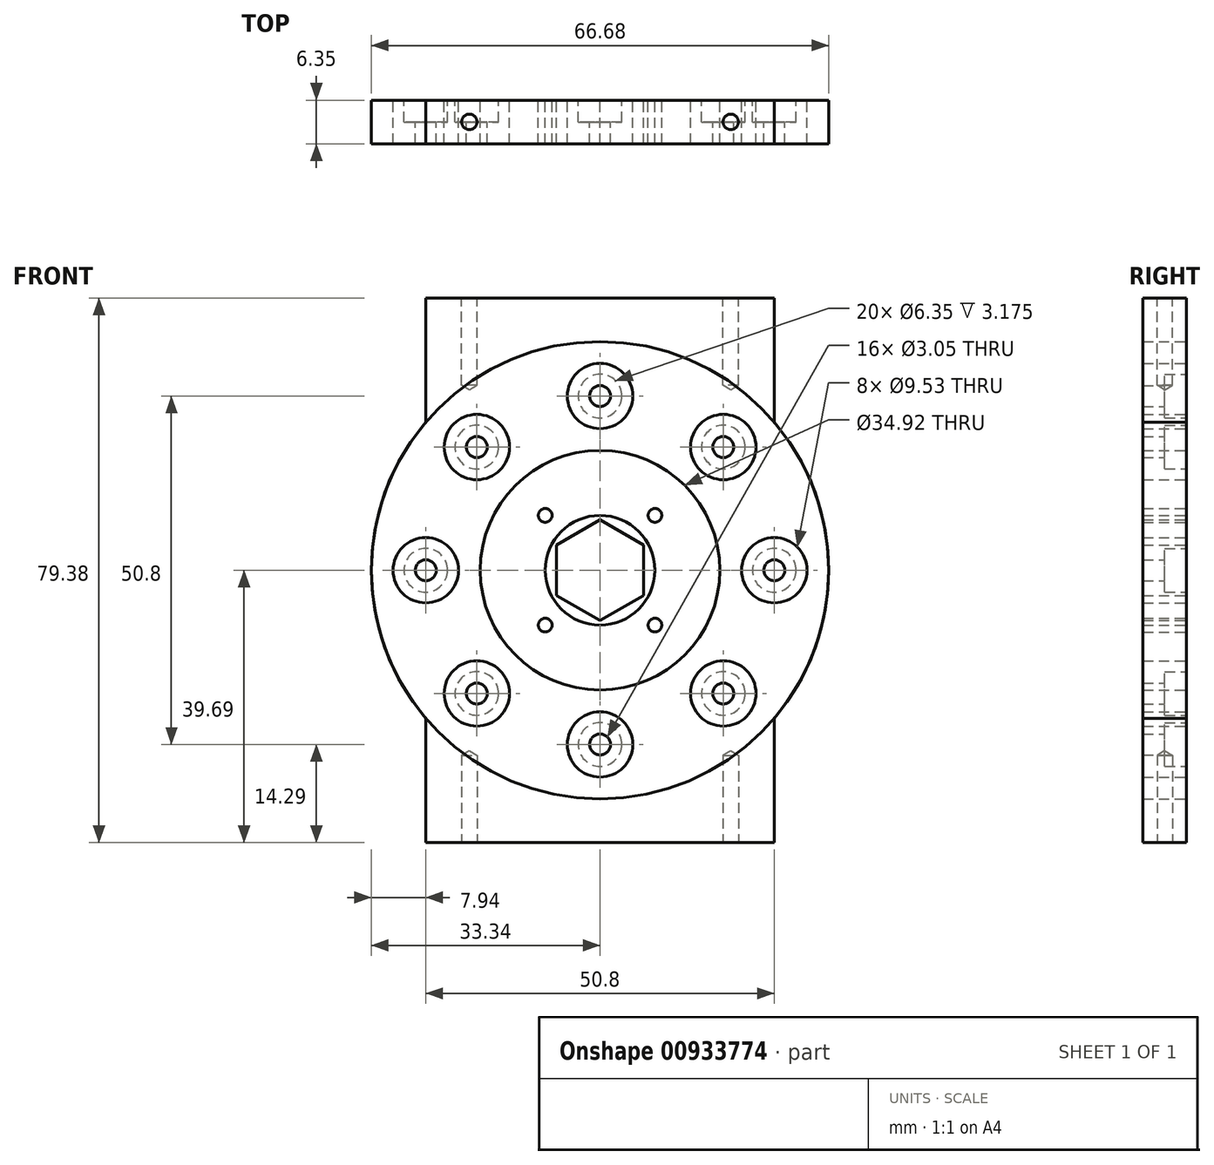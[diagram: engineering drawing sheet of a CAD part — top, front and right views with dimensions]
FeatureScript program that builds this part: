
annotation { "Feature Type Name" : "Feature", "Feature Type Description" : "" }
export const myFeature = defineFeature(function(context is Context, id is Id, definition is map)
    precondition{}
    {
        {
            var Q0;
            Q0=qCreatedBy(makeId("Top.planeOp"),FACE);
            cPlane(context, id + "F0", {"entities" : qUnion([Q0]), "cplaneType" : CPlaneType.OFFSET, "offset" : 39.69 * mm, "width" : 152.4 * mm, "height" : 152.4 * mm});
        }
        {
            var Q0;
            Q0=qCreatedBy(id+"F0.planeOp",FACE);
            cPlane(context, id + "F1", {"entities" : qUnion([Q0]), "cplaneType" : CPlaneType.OFFSET, "offset" : 79.38 * mm, "oppositeDirection" : true, "width" : 152.4 * mm, "height" : 152.4 * mm});
        }
        {
            var Q0;
            Q0=qCreatedBy(makeId("Front.planeOp"),FACE);
            var sketch = newSketch(context, id + "F2", { "sketchPlane" : qUnion([Q0])});
            skCircle(sketch, "E0", {"center": v(0, 0) * mm, "radius": 25.4 * mm, "construction": true});
            skPoint(sketch, "E1", {"position": v(-25.4, 0) * mm});
            skPoint(sketch, "E2.1.0", {"position": v(-17.96, -17.96) * mm});
            skPoint(sketch, "E2.2.0", {"position": v(0, -25.4) * mm});
            skPoint(sketch, "E2.3.0", {"position": v(17.96, -17.96) * mm});
            skPoint(sketch, "E2.4.0", {"position": v(25.4, 0) * mm});
            skPoint(sketch, "E2.5.0", {"position": v(17.96, 17.96) * mm});
            skPoint(sketch, "E2.6.0", {"position": v(0, 25.4) * mm});
            skPoint(sketch, "E2.7.0", {"position": v(-17.96, 17.96) * mm});
            skCircle(sketch, "E3", {"center": v(-17.96, 17.96) * mm, "radius": 3.18 * mm});
            skCircle(sketch, "E4", {"center": v(0, 25.4) * mm, "radius": 3.18 * mm});
            skCircle(sketch, "E5", {"center": v(17.96, 17.96) * mm, "radius": 3.18 * mm});
            skCircle(sketch, "E6", {"center": v(25.4, 0) * mm, "radius": 3.18 * mm});
            skCircle(sketch, "E7", {"center": v(17.96, -17.96) * mm, "radius": 3.18 * mm});
            skCircle(sketch, "E8", {"center": v(0, -25.4) * mm, "radius": 3.18 * mm});
            skCircle(sketch, "E9", {"center": v(-17.96, -17.96) * mm, "radius": 3.18 * mm});
            skCircle(sketch, "E10", {"center": v(-25.4, 0) * mm, "radius": 3.18 * mm});
            skCircle(sketch, "E11", {"center": v(-25.4, 0) * mm, "radius": 4.76 * mm});
            skCircle(sketch, "E12", {"center": v(-17.96, 17.96) * mm, "radius": 4.76 * mm});
            skCircle(sketch, "E13", {"center": v(0, 25.4) * mm, "radius": 4.76 * mm});
            skCircle(sketch, "E14", {"center": v(17.96, 17.96) * mm, "radius": 4.76 * mm});
            skCircle(sketch, "E15", {"center": v(25.4, 0) * mm, "radius": 4.76 * mm});
            skCircle(sketch, "E16", {"center": v(17.96, -17.96) * mm, "radius": 4.76 * mm});
            skCircle(sketch, "E17", {"center": v(0, -25.4) * mm, "radius": 4.76 * mm});
            skCircle(sketch, "E18", {"center": v(-17.96, -17.96) * mm, "radius": 4.76 * mm});
            skCircle(sketch, "E19", {"center": v(0, 0) * mm, "radius": 33.34 * mm});
            skCircle(sketch, "E20", {"center": v(0, 0) * mm, "radius": 17.46 * mm});
            skLineSegment(sketch, "E21", {"start": v(-25.4, -21.6) * mm, "end": v(-25.4, -39.69) * mm});
            skLineSegment(sketch, "E22", {"start": v(-25.4, -39.69) * mm, "end": v(25.4, -39.69) * mm});
            skLineSegment(sketch, "E23", {"start": v(25.4, -39.69) * mm, "end": v(25.4, -21.6) * mm});
            skPoint(sketch, "E24", {"position": v(0, -39.69) * mm});
            skLineSegment(sketch, "E25", {"start": v(25.4, 21.6) * mm, "end": v(25.4, 39.69) * mm});
            skLineSegment(sketch, "E26", {"start": v(25.4, 39.69) * mm, "end": v(-25.4, 39.69) * mm});
            skLineSegment(sketch, "E27", {"start": v(-25.4, 39.69) * mm, "end": v(-25.4, 21.6) * mm});
            skCircle(sketch, "E28", {"center": v(0, 0) * mm, "radius": 8 * mm});
            skCircle(sketch, "E29", {"center": v(-8, 8) * mm, "radius": 1 * mm});
            skCircle(sketch, "E30", {"center": v(-8, -8) * mm, "radius": 1 * mm});
            skCircle(sketch, "E31", {"center": v(8, -8) * mm, "radius": 1 * mm});
            skCircle(sketch, "E32", {"center": v(8, 8) * mm, "radius": 1 * mm});
            skLineSegment(sketch, "E33", {"start": v(-8, 8) * mm, "end": v(-8, -8) * mm, "construction": true});
            skLineSegment(sketch, "E34", {"start": v(-8, -8) * mm, "end": v(8, -8) * mm, "construction": true});
            skLineSegment(sketch, "E35", {"start": v(8, -8) * mm, "end": v(8, 8) * mm, "construction": true});
            skLineSegment(sketch, "E36", {"start": v(8, 8) * mm, "end": v(-8, 8) * mm, "construction": true});
            skPoint(sketch, "E37", {"position": v(0, 8) * mm});
            skPoint(sketch, "E38", {"position": v(8, 0) * mm});
            skCircle(sketch, "E39.cCircle", {"center": v(0, 0) * mm, "radius": 6.35 * mm, "construction": true});
            skLineSegment(sketch, "E39.0", {"start": v(6.35, 3.67) * mm, "end": v(6.35, -3.67) * mm});
            skLineSegment(sketch, "E39.1", {"start": v(6.35, -3.67) * mm, "end": v(0, -7.33) * mm});
            skLineSegment(sketch, "E39.2", {"start": v(0, -7.33) * mm, "end": v(-6.35, -3.67) * mm});
            skLineSegment(sketch, "E39.3", {"start": v(-6.35, -3.67) * mm, "end": v(-6.35, 3.67) * mm});
            skLineSegment(sketch, "E39.4", {"start": v(-6.35, 3.67) * mm, "end": v(0, 7.33) * mm});
            skLineSegment(sketch, "E39.5", {"start": v(0, 7.33) * mm, "end": v(6.35, 3.67) * mm});
            skPoint(sketch, "E39.0.midPoint", {"position": v(6.35, 0) * mm});
            skSolve(sketch);
        }
        {
            var Q0;
            Q0=qCreatedBy(id+"F0.planeOp",FACE);
            var sketch = newSketch(context, id + "F3", { "sketchPlane" : qUnion([Q0])});
            skLineSegment(sketch, "E40.bottom", {"start": v(-25.4, 0) * mm, "end": v(25.4, 0) * mm});
            skLineSegment(sketch, "E40.top", {"start": v(-25.4, -6.35) * mm, "end": v(25.4, -6.35) * mm});
            skLineSegment(sketch, "E40.left", {"start": v(-25.4, 0) * mm, "end": v(-25.4, -6.35) * mm});
            skLineSegment(sketch, "E40.right", {"start": v(25.4, 0) * mm, "end": v(25.4, -6.35) * mm});
            skPoint(sketch, "E41", {"position": v(-25.4, -3.17) * mm});
            skPoint(sketch, "E42", {"position": v(-19.05, -3.17) * mm});
            skPoint(sketch, "E43", {"position": v(25.4, -3.17) * mm});
            skPoint(sketch, "E44", {"position": v(19.05, -3.17) * mm});
            skSolve(sketch);
        }
        {
            var Q0;
            Q0=qCreatedBy(id+"F1.planeOp",FACE);
            var sketch = newSketch(context, id + "F4", { "sketchPlane" : qUnion([Q0])});
            skPoint(sketch, "E45", {"position": v(-19.05, -3.17) * mm});
            skPoint(sketch, "E46", {"position": v(19.05, -3.17) * mm});
            skSolve(sketch);
        }
        {
            var Q0;
            {var subQ0=sQuery(id+"F2.wireOp",EDGE,"E21");Q0=makeQuery(id+"F2.imprint","IMPRINT",FACE,{"disambiguationData":[TD([[makeQuery(id+"F2.imprint","IMPRINT",EDGE,{"derivedFrom":subQ0}),1.0]])]});}
            var Q1;
            Q1=makeQuery(id+"F2.imprint","IMPRINT",FACE,{"disambiguationData":[TD([[makeQuery(id+"F2.imprint","IMPRINT",EDGE,{"derivedFrom":sQuery(id+"F2.wireOp",EDGE,"E11")}),-1.0]])]});
            var Q2;
            Q2=makeQuery(id+"F2.imprint","IMPRINT",FACE,{"disambiguationData":[TD([[makeQuery(id+"F2.imprint","IMPRINT",EDGE,{"derivedFrom":sQuery(id+"F2.wireOp",EDGE,"E8")}),1.0]])]});
            var Q3;
            Q3=makeQuery(id+"F2.imprint","IMPRINT",FACE,{"disambiguationData":[TD([[makeQuery(id+"F2.imprint","IMPRINT",EDGE,{"derivedFrom":sQuery(id+"F2.wireOp",EDGE,"E8")}),-1.0]])]});
            var Q4;
            Q4=makeQuery(id+"F2.imprint","IMPRINT",FACE,{"disambiguationData":[TD([[makeQuery(id+"F2.imprint","IMPRINT",EDGE,{"derivedFrom":sQuery(id+"F2.wireOp",EDGE,"E10")}),-1.0]])]});
            var Q5;
            Q5=makeQuery(id+"F2.imprint","IMPRINT",FACE,{"disambiguationData":[TD([[makeQuery(id+"F2.imprint","IMPRINT",EDGE,{"derivedFrom":sQuery(id+"F2.wireOp",EDGE,"E7")}),-1.0]])]});
            var Q6;
            Q6=makeQuery(id+"F2.imprint","IMPRINT",FACE,{"disambiguationData":[TD([[makeQuery(id+"F2.imprint","IMPRINT",EDGE,{"derivedFrom":sQuery(id+"F2.wireOp",EDGE,"E6")}),-1.0]])]});
            var Q7;
            Q7=makeQuery(id+"F2.imprint","IMPRINT",FACE,{"disambiguationData":[TD([[makeQuery(id+"F2.imprint","IMPRINT",EDGE,{"derivedFrom":sQuery(id+"F2.wireOp",EDGE,"E5")}),-1.0]])]});
            var Q8;
            Q8=makeQuery(id+"F2.imprint","IMPRINT",FACE,{"disambiguationData":[TD([[makeQuery(id+"F2.imprint","IMPRINT",EDGE,{"derivedFrom":sQuery(id+"F2.wireOp",EDGE,"E4")}),-1.0]])]});
            var Q9;
            Q9=makeQuery(id+"F2.imprint","IMPRINT",FACE,{"disambiguationData":[TD([[makeQuery(id+"F2.imprint","IMPRINT",EDGE,{"derivedFrom":sQuery(id+"F2.wireOp",EDGE,"E3")}),-1.0]])]});
            var Q10;
            Q10=makeQuery(id+"F2.imprint","IMPRINT",FACE,{"disambiguationData":[TD([[makeQuery(id+"F2.imprint","IMPRINT",EDGE,{"derivedFrom":sQuery(id+"F2.wireOp",EDGE,"E7")}),1.0]])]});
            var Q11;
            Q11=makeQuery(id+"F2.imprint","IMPRINT",FACE,{"disambiguationData":[TD([[makeQuery(id+"F2.imprint","IMPRINT",EDGE,{"derivedFrom":sQuery(id+"F2.wireOp",EDGE,"E6")}),1.0]])]});
            var Q12;
            Q12=makeQuery(id+"F2.imprint","IMPRINT",FACE,{"disambiguationData":[TD([[makeQuery(id+"F2.imprint","IMPRINT",EDGE,{"derivedFrom":sQuery(id+"F2.wireOp",EDGE,"E10")}),1.0]])]});
            var Q13;
            Q13=makeQuery(id+"F2.imprint","IMPRINT",FACE,{"disambiguationData":[TD([[makeQuery(id+"F2.imprint","IMPRINT",EDGE,{"derivedFrom":sQuery(id+"F2.wireOp",EDGE,"E9")}),-1.0]])]});
            var Q14;
            Q14=makeQuery(id+"F2.imprint","IMPRINT",FACE,{"disambiguationData":[TD([[makeQuery(id+"F2.imprint","IMPRINT",EDGE,{"derivedFrom":sQuery(id+"F2.wireOp",EDGE,"E3")}),1.0]])]});
            var Q15;
            Q15=makeQuery(id+"F2.imprint","IMPRINT",FACE,{"disambiguationData":[TD([[makeQuery(id+"F2.imprint","IMPRINT",EDGE,{"derivedFrom":sQuery(id+"F2.wireOp",EDGE,"E9")}),1.0]])]});
            var Q16;
            Q16=makeQuery(id+"F2.imprint","IMPRINT",FACE,{"disambiguationData":[TD([[makeQuery(id+"F2.imprint","IMPRINT",EDGE,{"derivedFrom":sQuery(id+"F2.wireOp",EDGE,"E4")}),1.0]])]});
            var Q17;
            Q17=makeQuery(id+"F2.imprint","IMPRINT",FACE,{"disambiguationData":[TD([[makeQuery(id+"F2.imprint","IMPRINT",EDGE,{"derivedFrom":sQuery(id+"F2.wireOp",EDGE,"E5")}),1.0]])]});
            var Q18;
            {var subQ0=sQuery(id+"F2.wireOp",EDGE,"E25");Q18=makeQuery(id+"F2.imprint","IMPRINT",FACE,{"disambiguationData":[TD([[makeQuery(id+"F2.imprint","IMPRINT",EDGE,{"derivedFrom":subQ0}),1.0]])]});}
            extrude(context, id + "F5", {"entities" : qUnion([Q0, Q1, Q2, Q3, Q4, Q5, Q6, Q7, Q8, Q9, Q10, Q11, Q12, Q13, Q14, Q15, Q16, Q17, Q18]), "depth" : 6.35 * mm, "offsetDistance" : 25.4 * mm});
        }
        {
            var Q0;
            Q0=makeQuery(id+"F2.imprint","IMPRINT",FACE,{"disambiguationData":[TD([[makeQuery(id+"F2.imprint","IMPRINT",EDGE,{"derivedFrom":sQuery(id+"F2.wireOp",EDGE,"E7")}),1.0]])]});
            var Q1;
            Q1=makeQuery(id+"F2.imprint","IMPRINT",FACE,{"disambiguationData":[TD([[makeQuery(id+"F2.imprint","IMPRINT",EDGE,{"derivedFrom":sQuery(id+"F2.wireOp",EDGE,"E5")}),1.0]])]});
            var Q2;
            Q2=makeQuery(id+"F2.imprint","IMPRINT",FACE,{"disambiguationData":[TD([[makeQuery(id+"F2.imprint","IMPRINT",EDGE,{"derivedFrom":sQuery(id+"F2.wireOp",EDGE,"E3")}),1.0]])]});
            var Q3;
            Q3=makeQuery(id+"F2.imprint","IMPRINT",FACE,{"disambiguationData":[TD([[makeQuery(id+"F2.imprint","IMPRINT",EDGE,{"derivedFrom":sQuery(id+"F2.wireOp",EDGE,"E9")}),1.0]])]});
            var Q4;
            Q4=sQuery(id+"F2.wireOp",EDGE,"E9");
            var Q5;
            Q5=sQuery(id+"F2.wireOp",EDGE,"E3");
            var Q6;
            Q6=sQuery(id+"F2.wireOp",EDGE,"E5");
            var Q7;
            Q7=sQuery(id+"F2.wireOp",EDGE,"E7");
            extrude(context, id + "F6", {"entities" : qUnion([Q0, Q1, Q2, Q3]), "operationType" : NewBodyOperationType.REMOVE, "surfaceEntities" : qUnion([Q4, Q5, Q6, Q7]), "depth" : 3.17 * mm, "offsetDistance" : 25.4 * mm});
        }
        {
            var Q0;
            Q0=sQuery(id+"F2.wireOp",VERTEX,"E2.5.0");
            var Q1;
            Q1=sQuery(id+"F2.wireOp",VERTEX,"E2.7.0");
            var Q2;
            Q2=sQuery(id+"F2.wireOp",VERTEX,"E2.1.0");
            var Q3;
            Q3=sQuery(id+"F2.wireOp",VERTEX,"E2.3.0");
            var Q4;
            Q4=makeQuery(id+"F5.opExtrude","SWEPT_BODY",BODY,{"disambiguationData":[OSD([sQuery(id+"F2.wireOp",EDGE,"E19"),sQuery(id+"F2.wireOp",EDGE,"E20"),sQuery(id+"F2.wireOp",EDGE,"E21"),sQuery(id+"F2.wireOp",EDGE,"E22"),sQuery(id+"F2.wireOp",EDGE,"E23"),sQuery(id+"F2.wireOp",EDGE,"E25"),sQuery(id+"F2.wireOp",EDGE,"E26"),sQuery(id+"F2.wireOp",EDGE,"E27")])]});
            hole(context, id + "F7", {"style" : HoleStyle.SIMPLE, "endStyle" : HoleEndStyle.THROUGH, "oppositeDirection" : true, "standardTappedOrClearance" : lookupTablePath({ "fit" : "Close (ASME)", "standard" : "ANSI", "size" : "#4", "type" : "Clearance" }), "standardBlindInLast" : lookupTablePath({ "fit" : "Close", "standard" : "ANSI", "engagement" : "75%", "pitch" : "40 tpi", "size" : "#4", "type" : "Clearance & tapped" }), "holeDiameter" : 3.05 * mm, "majorDiameter" : 6.35 * mm, "isTappedThrough" : true, "tappedDepth" : 12.7 * mm, "tapClearance" : 3, "locations" : qUnion([Q0, Q1, Q2, Q3]), "scope" : qUnion([Q4])});
        }
        {
            var Q0;
            Q0=sQuery(id+"F3.wireOp",VERTEX,"E42");
            var Q1;
            Q1=sQuery(id+"F3.wireOp",VERTEX,"E44");
            var Q2;
            Q2=makeQuery(id+"F5.opExtrude","SWEPT_BODY",BODY,{"disambiguationData":[OSD([sQuery(id+"F2.wireOp",EDGE,"E19"),sQuery(id+"F2.wireOp",EDGE,"E20"),sQuery(id+"F2.wireOp",EDGE,"E21"),sQuery(id+"F2.wireOp",EDGE,"E22"),sQuery(id+"F2.wireOp",EDGE,"E23"),sQuery(id+"F2.wireOp",EDGE,"E25"),sQuery(id+"F2.wireOp",EDGE,"E26"),sQuery(id+"F2.wireOp",EDGE,"E27")])]});
            hole(context, id + "F8", {"style" : HoleStyle.SIMPLE, "endStyle" : HoleEndStyle.BLIND, "standardTappedOrClearance" : lookupTablePath({ "standard" : "ANSI", "engagement" : "75%", "pitch" : "40 tpi", "size" : "#4", "type" : "Tapped" }), "standardBlindInLast" : lookupTablePath({ "standard" : "ANSI", "fit" : "Normal", "engagement" : "75%", "pitch" : "40 tpi", "size" : "#4", "type" : "Clearance & tapped" }), "holeDiameter" : 2.26 * mm, "majorDiameter" : 2.84 * mm, "showTappedDepth" : true, "holeDepth" : 12.7 * mm, "isTappedThrough" : true, "tappedDepth" : 10.8 * mm, "tapClearance" : 3, "locations" : qUnion([Q0, Q1]), "scope" : qUnion([Q2])});
        }
        {
            var Q0;
            Q0=sQuery(id+"F4.wireOp",VERTEX,"E45");
            var Q1;
            Q1=sQuery(id+"F4.wireOp",VERTEX,"E46");
            var Q2;
            Q2=makeQuery(id+"F5.opExtrude","SWEPT_BODY",BODY,{"disambiguationData":[OSD([sQuery(id+"F2.wireOp",EDGE,"E19"),sQuery(id+"F2.wireOp",EDGE,"E20"),sQuery(id+"F2.wireOp",EDGE,"E21"),sQuery(id+"F2.wireOp",EDGE,"E22"),sQuery(id+"F2.wireOp",EDGE,"E23"),sQuery(id+"F2.wireOp",EDGE,"E25"),sQuery(id+"F2.wireOp",EDGE,"E26"),sQuery(id+"F2.wireOp",EDGE,"E27")])]});
            hole(context, id + "F9", {"style" : HoleStyle.SIMPLE, "endStyle" : HoleEndStyle.BLIND, "oppositeDirection" : true, "standardTappedOrClearance" : lookupTablePath({ "standard" : "ANSI", "engagement" : "75%", "pitch" : "40 tpi", "size" : "#4", "type" : "Tapped" }), "standardBlindInLast" : lookupTablePath({ "standard" : "ANSI", "fit" : "Normal", "engagement" : "75%", "pitch" : "40 tpi", "size" : "#4", "type" : "Clearance & tapped" }), "holeDiameter" : 2.26 * mm, "majorDiameter" : 2.84 * mm, "showTappedDepth" : true, "holeDepth" : 12.7 * mm, "isTappedThrough" : true, "tappedDepth" : 10.8 * mm, "tapClearance" : 3, "locations" : qUnion([Q0, Q1]), "scope" : qUnion([Q2])});
        }
        {
            var Q0;
            Q0=makeQuery(id+"F2.imprint","IMPRINT",FACE,{"disambiguationData":[TD([[makeQuery(id+"F2.imprint","IMPRINT",EDGE,{"derivedFrom":sQuery(id+"F2.wireOp",EDGE,"E10")}),1.0]])]});
            var Q1;
            Q1=makeQuery(id+"F2.imprint","IMPRINT",FACE,{"disambiguationData":[TD([[makeQuery(id+"F2.imprint","IMPRINT",EDGE,{"derivedFrom":sQuery(id+"F2.wireOp",EDGE,"E10")}),-1.0]])]});
            var Q2;
            Q2=makeQuery(id+"F2.imprint","IMPRINT",FACE,{"disambiguationData":[TD([[makeQuery(id+"F2.imprint","IMPRINT",EDGE,{"derivedFrom":sQuery(id+"F2.wireOp",EDGE,"E8")}),1.0]])]});
            var Q3;
            Q3=makeQuery(id+"F2.imprint","IMPRINT",FACE,{"disambiguationData":[TD([[makeQuery(id+"F2.imprint","IMPRINT",EDGE,{"derivedFrom":sQuery(id+"F2.wireOp",EDGE,"E8")}),-1.0]])]});
            var Q4;
            Q4=makeQuery(id+"F2.imprint","IMPRINT",FACE,{"disambiguationData":[TD([[makeQuery(id+"F2.imprint","IMPRINT",EDGE,{"derivedFrom":sQuery(id+"F2.wireOp",EDGE,"E6")}),-1.0]])]});
            var Q5;
            Q5=makeQuery(id+"F2.imprint","IMPRINT",FACE,{"disambiguationData":[TD([[makeQuery(id+"F2.imprint","IMPRINT",EDGE,{"derivedFrom":sQuery(id+"F2.wireOp",EDGE,"E6")}),1.0]])]});
            var Q6;
            Q6=makeQuery(id+"F2.imprint","IMPRINT",FACE,{"disambiguationData":[TD([[makeQuery(id+"F2.imprint","IMPRINT",EDGE,{"derivedFrom":sQuery(id+"F2.wireOp",EDGE,"E4")}),1.0]])]});
            var Q7;
            Q7=makeQuery(id+"F2.imprint","IMPRINT",FACE,{"disambiguationData":[TD([[makeQuery(id+"F2.imprint","IMPRINT",EDGE,{"derivedFrom":sQuery(id+"F2.wireOp",EDGE,"E4")}),-1.0]])]});
            var Q8;
            Q8=makeQuery(id+"F2.imprint","IMPRINT",FACE,{"disambiguationData":[TD([[makeQuery(id+"F2.imprint","IMPRINT",EDGE,{"derivedFrom":sQuery(id+"F2.wireOp",EDGE,"E11")}),-1.0]])]});
            var Q9;
            Q9=makeQuery(id+"F2.imprint","IMPRINT",FACE,{"disambiguationData":[TD([[makeQuery(id+"F2.imprint","IMPRINT",EDGE,{"derivedFrom":sQuery(id+"F2.wireOp",EDGE,"E20")}),1.0]])]});
            extrude(context, id + "F10", {"entities" : qUnion([Q0, Q1, Q2, Q3, Q4, Q5, Q6, Q7, Q8, Q9]), "depth" : 6.35 * mm, "offsetDistance" : 25.4 * mm});
        }
        {
            var Q0;
            Q0=makeQuery(id+"F2.imprint","IMPRINT",FACE,{"disambiguationData":[TD([[makeQuery(id+"F2.imprint","IMPRINT",EDGE,{"derivedFrom":sQuery(id+"F2.wireOp",EDGE,"E4")}),1.0]])]});
            var Q1;
            Q1=makeQuery(id+"F2.imprint","IMPRINT",FACE,{"disambiguationData":[TD([[makeQuery(id+"F2.imprint","IMPRINT",EDGE,{"derivedFrom":sQuery(id+"F2.wireOp",EDGE,"E10")}),1.0]])]});
            var Q2;
            Q2=makeQuery(id+"F2.imprint","IMPRINT",FACE,{"disambiguationData":[TD([[makeQuery(id+"F2.imprint","IMPRINT",EDGE,{"derivedFrom":sQuery(id+"F2.wireOp",EDGE,"E8")}),1.0]])]});
            var Q3;
            Q3=makeQuery(id+"F2.imprint","IMPRINT",FACE,{"disambiguationData":[TD([[makeQuery(id+"F2.imprint","IMPRINT",EDGE,{"derivedFrom":sQuery(id+"F2.wireOp",EDGE,"E6")}),1.0]])]});
            var Q4;
            Q4=sQuery(id+"F2.wireOp",EDGE,"E10");
            var Q5;
            Q5=sQuery(id+"F2.wireOp",EDGE,"E6");
            var Q6;
            Q6=sQuery(id+"F2.wireOp",EDGE,"E8");
            var Q7;
            Q7=sQuery(id+"F2.wireOp",EDGE,"E4");
            extrude(context, id + "F11", {"entities" : qUnion([Q0, Q1, Q2, Q3]), "operationType" : NewBodyOperationType.REMOVE, "surfaceEntities" : qUnion([Q4, Q5, Q6, Q7]), "depth" : 3.17 * mm, "offsetDistance" : 25.4 * mm});
        }
        {
            var Q0;
            Q0=sQuery(id+"F2.wireOp",VERTEX,"E2.4.0");
            var Q1;
            Q1=sQuery(id+"F2.wireOp",VERTEX,"E2.6.0");
            var Q2;
            Q2=sQuery(id+"F2.wireOp",VERTEX,"E1");
            var Q3;
            Q3=sQuery(id+"F2.wireOp",VERTEX,"E2.2.0");
            var Q4;
            Q4=makeQuery(id+"F10.opExtrude","SWEPT_BODY",BODY,{"disambiguationData":[OSD([sQuery(id+"F2.wireOp",EDGE,"E12"),sQuery(id+"F2.wireOp",EDGE,"E14"),sQuery(id+"F2.wireOp",EDGE,"E16"),sQuery(id+"F2.wireOp",EDGE,"E18"),sQuery(id+"F2.wireOp",EDGE,"E19"),sQuery(id+"F2.wireOp",EDGE,"E28"),sQuery(id+"F2.wireOp",EDGE,"E29"),sQuery(id+"F2.wireOp",EDGE,"E30"),sQuery(id+"F2.wireOp",EDGE,"E31"),sQuery(id+"F2.wireOp",EDGE,"E32")])]});
            hole(context, id + "F12", {"style" : HoleStyle.SIMPLE, "endStyle" : HoleEndStyle.THROUGH, "oppositeDirection" : true, "standardTappedOrClearance" : lookupTablePath({ "fit" : "Close (ASME)", "standard" : "ANSI", "size" : "#4", "type" : "Clearance" }), "standardBlindInLast" : lookupTablePath({ "fit" : "Close", "standard" : "ANSI", "engagement" : "75%", "pitch" : "40 tpi", "size" : "#4", "type" : "Clearance & tapped" }), "holeDiameter" : 3.05 * mm, "majorDiameter" : 6.35 * mm, "isTappedThrough" : true, "tappedDepth" : 12.7 * mm, "tapClearance" : 3, "locations" : qUnion([Q0, Q1, Q2, Q3]), "scope" : qUnion([Q4])});
        }
        {
            var Q0;
            {var subQ0=sQuery(id+"F2.wireOp",EDGE,"E25");Q0=makeQuery(id+"F2.imprint","IMPRINT",FACE,{"disambiguationData":[TD([[makeQuery(id+"F2.imprint","IMPRINT",EDGE,{"derivedFrom":subQ0}),1.0]])]});}
            var Q1;
            Q1=makeQuery(id+"F2.imprint","IMPRINT",FACE,{"disambiguationData":[TD([[makeQuery(id+"F2.imprint","IMPRINT",EDGE,{"derivedFrom":sQuery(id+"F2.wireOp",EDGE,"E11")}),-1.0]])]});
            var Q2;
            Q2=makeQuery(id+"F2.imprint","IMPRINT",FACE,{"disambiguationData":[TD([[makeQuery(id+"F2.imprint","IMPRINT",EDGE,{"derivedFrom":sQuery(id+"F2.wireOp",EDGE,"E5")}),-1.0]])]});
            var Q3;
            Q3=makeQuery(id+"F2.imprint","IMPRINT",FACE,{"disambiguationData":[TD([[makeQuery(id+"F2.imprint","IMPRINT",EDGE,{"derivedFrom":sQuery(id+"F2.wireOp",EDGE,"E5")}),1.0]])]});
            var Q4;
            Q4=makeQuery(id+"F2.imprint","IMPRINT",FACE,{"disambiguationData":[TD([[makeQuery(id+"F2.imprint","IMPRINT",EDGE,{"derivedFrom":sQuery(id+"F2.wireOp",EDGE,"E28")}),1.0]])]});
            var Q5;
            Q5=makeQuery(id+"F2.imprint","IMPRINT",FACE,{"disambiguationData":[TD([[makeQuery(id+"F2.imprint","IMPRINT",EDGE,{"derivedFrom":sQuery(id+"F2.wireOp",EDGE,"E20")}),1.0]])]});
            var Q6;
            Q6=makeQuery(id+"F2.imprint","IMPRINT",FACE,{"disambiguationData":[TD([[makeQuery(id+"F2.imprint","IMPRINT",EDGE,{"derivedFrom":sQuery(id+"F2.wireOp",EDGE,"E7")}),1.0]])]});
            var Q7;
            Q7=makeQuery(id+"F2.imprint","IMPRINT",FACE,{"disambiguationData":[TD([[makeQuery(id+"F2.imprint","IMPRINT",EDGE,{"derivedFrom":sQuery(id+"F2.wireOp",EDGE,"E7")}),-1.0]])]});
            var Q8;
            Q8=makeQuery(id+"F2.imprint","IMPRINT",FACE,{"disambiguationData":[TD([[makeQuery(id+"F2.imprint","IMPRINT",EDGE,{"derivedFrom":sQuery(id+"F2.wireOp",EDGE,"E9")}),-1.0]])]});
            var Q9;
            {var subQ0=sQuery(id+"F2.wireOp",EDGE,"E21");Q9=makeQuery(id+"F2.imprint","IMPRINT",FACE,{"disambiguationData":[TD([[makeQuery(id+"F2.imprint","IMPRINT",EDGE,{"derivedFrom":subQ0}),1.0]])]});}
            var Q10;
            Q10=makeQuery(id+"F2.imprint","IMPRINT",FACE,{"disambiguationData":[TD([[makeQuery(id+"F2.imprint","IMPRINT",EDGE,{"derivedFrom":sQuery(id+"F2.wireOp",EDGE,"E3")}),-1.0]])]});
            var Q11;
            Q11=makeQuery(id+"F2.imprint","IMPRINT",FACE,{"disambiguationData":[TD([[makeQuery(id+"F2.imprint","IMPRINT",EDGE,{"derivedFrom":sQuery(id+"F2.wireOp",EDGE,"E3")}),1.0]])]});
            var Q12;
            Q12=makeQuery(id+"F2.imprint","IMPRINT",FACE,{"disambiguationData":[TD([[makeQuery(id+"F2.imprint","IMPRINT",EDGE,{"derivedFrom":sQuery(id+"F2.wireOp",EDGE,"E9")}),1.0]])]});
            var Q13;
            Q13=makeQuery(id+"F2.imprint","IMPRINT",FACE,{"disambiguationData":[TD([[makeQuery(id+"F2.imprint","IMPRINT",EDGE,{"derivedFrom":sQuery(id+"F2.wireOp",EDGE,"E31")}),1.0]])]});
            var Q14;
            Q14=makeQuery(id+"F2.imprint","IMPRINT",FACE,{"disambiguationData":[TD([[makeQuery(id+"F2.imprint","IMPRINT",EDGE,{"derivedFrom":sQuery(id+"F2.wireOp",EDGE,"E29")}),1.0]])]});
            var Q15;
            Q15=makeQuery(id+"F2.imprint","IMPRINT",FACE,{"disambiguationData":[TD([[makeQuery(id+"F2.imprint","IMPRINT",EDGE,{"derivedFrom":sQuery(id+"F2.wireOp",EDGE,"E32")}),1.0]])]});
            var Q16;
            Q16=makeQuery(id+"F2.imprint","IMPRINT",FACE,{"disambiguationData":[TD([[makeQuery(id+"F2.imprint","IMPRINT",EDGE,{"derivedFrom":sQuery(id+"F2.wireOp",EDGE,"E30")}),1.0]])]});
            extrude(context, id + "F13", {"entities" : qUnion([Q0, Q1, Q2, Q3, Q4, Q5, Q6, Q7, Q8, Q9, Q10, Q11, Q12, Q13, Q14, Q15, Q16]), "depth" : 6.35 * mm, "offsetDistance" : 25.4 * mm});
        }
        {
            var Q0;
            Q0=makeQuery(id+"F2.imprint","IMPRINT",FACE,{"disambiguationData":[TD([[makeQuery(id+"F2.imprint","IMPRINT",EDGE,{"derivedFrom":sQuery(id+"F2.wireOp",EDGE,"E7")}),1.0]])]});
            var Q1;
            Q1=makeQuery(id+"F2.imprint","IMPRINT",FACE,{"disambiguationData":[TD([[makeQuery(id+"F2.imprint","IMPRINT",EDGE,{"derivedFrom":sQuery(id+"F2.wireOp",EDGE,"E5")}),1.0]])]});
            var Q2;
            Q2=makeQuery(id+"F2.imprint","IMPRINT",FACE,{"disambiguationData":[TD([[makeQuery(id+"F2.imprint","IMPRINT",EDGE,{"derivedFrom":sQuery(id+"F2.wireOp",EDGE,"E3")}),1.0]])]});
            var Q3;
            Q3=makeQuery(id+"F2.imprint","IMPRINT",FACE,{"disambiguationData":[TD([[makeQuery(id+"F2.imprint","IMPRINT",EDGE,{"derivedFrom":sQuery(id+"F2.wireOp",EDGE,"E9")}),1.0]])]});
            extrude(context, id + "F14", {"entities" : qUnion([Q0, Q1, Q2, Q3]), "operationType" : NewBodyOperationType.REMOVE, "depth" : 3.17 * mm, "offsetDistance" : 25.4 * mm});
        }
        {
            var Q0;
            Q0=sQuery(id+"F2.wireOp",VERTEX,"E2.5.0");
            var Q1;
            Q1=sQuery(id+"F2.wireOp",VERTEX,"E2.7.0");
            var Q2;
            Q2=sQuery(id+"F2.wireOp",VERTEX,"E2.1.0");
            var Q3;
            Q3=sQuery(id+"F2.wireOp",VERTEX,"E2.3.0");
            var Q4;
            Q4=makeQuery(id+"F13.opExtrude","SWEPT_BODY",BODY,{"disambiguationData":[OSD([sQuery(id+"F2.wireOp",EDGE,"E11"),sQuery(id+"F2.wireOp",EDGE,"E13"),sQuery(id+"F2.wireOp",EDGE,"E15"),sQuery(id+"F2.wireOp",EDGE,"E17"),sQuery(id+"F2.wireOp",EDGE,"E19"),sQuery(id+"F2.wireOp",EDGE,"E21"),sQuery(id+"F2.wireOp",EDGE,"E22"),sQuery(id+"F2.wireOp",EDGE,"E23"),sQuery(id+"F2.wireOp",EDGE,"E25"),sQuery(id+"F2.wireOp",EDGE,"E26"),sQuery(id+"F2.wireOp",EDGE,"E27")])]});
            hole(context, id + "F15", {"style" : HoleStyle.SIMPLE, "endStyle" : HoleEndStyle.THROUGH, "oppositeDirection" : true, "standardTappedOrClearance" : lookupTablePath({ "fit" : "Close (ASME)", "standard" : "ANSI", "size" : "#4", "type" : "Clearance" }), "standardBlindInLast" : lookupTablePath({ "fit" : "Close", "standard" : "ANSI", "engagement" : "75%", "pitch" : "40 tpi", "size" : "#4", "type" : "Clearance & tapped" }), "holeDiameter" : 3.05 * mm, "majorDiameter" : 6.35 * mm, "isTappedThrough" : true, "tappedDepth" : 12.7 * mm, "tapClearance" : 3, "locations" : qUnion([Q0, Q1, Q2, Q3]), "scope" : qUnion([Q4])});
        }
        {
            var Q0;
            Q0=sQuery(id+"F3.wireOp",VERTEX,"E42");
            var Q1;
            Q1=sQuery(id+"F3.wireOp",VERTEX,"E44");
            var Q2;
            Q2=makeQuery(id+"F13.opExtrude","SWEPT_BODY",BODY,{"disambiguationData":[OSD([sQuery(id+"F2.wireOp",EDGE,"E11"),sQuery(id+"F2.wireOp",EDGE,"E13"),sQuery(id+"F2.wireOp",EDGE,"E15"),sQuery(id+"F2.wireOp",EDGE,"E17"),sQuery(id+"F2.wireOp",EDGE,"E19"),sQuery(id+"F2.wireOp",EDGE,"E21"),sQuery(id+"F2.wireOp",EDGE,"E22"),sQuery(id+"F2.wireOp",EDGE,"E23"),sQuery(id+"F2.wireOp",EDGE,"E25"),sQuery(id+"F2.wireOp",EDGE,"E26"),sQuery(id+"F2.wireOp",EDGE,"E27"),sQuery(id+"F2.wireOp",EDGE,"E39.0"),sQuery(id+"F2.wireOp",EDGE,"E39.1"),sQuery(id+"F2.wireOp",EDGE,"E39.2"),sQuery(id+"F2.wireOp",EDGE,"E39.3"),sQuery(id+"F2.wireOp",EDGE,"E39.4"),sQuery(id+"F2.wireOp",EDGE,"E39.5")])]});
            hole(context, id + "F16", {"style" : HoleStyle.SIMPLE, "endStyle" : HoleEndStyle.BLIND, "standardTappedOrClearance" : lookupTablePath({ "standard" : "ANSI", "engagement" : "75%", "pitch" : "40 tpi", "size" : "#4", "type" : "Tapped" }), "standardBlindInLast" : lookupTablePath({ "standard" : "ANSI", "fit" : "Normal", "engagement" : "75%", "pitch" : "40 tpi", "size" : "#4", "type" : "Clearance & tapped" }), "holeDiameter" : 2.26 * mm, "majorDiameter" : 2.84 * mm, "showTappedDepth" : true, "holeDepth" : 12.7 * mm, "isTappedThrough" : true, "tappedDepth" : 10.8 * mm, "tapClearance" : 3, "locations" : qUnion([Q0, Q1]), "scope" : qUnion([Q2])});
        }
        {
            var Q0;
            Q0=sQuery(id+"F4.wireOp",VERTEX,"E45");
            var Q1;
            Q1=sQuery(id+"F4.wireOp",VERTEX,"E46");
            var Q2;
            Q2=makeQuery(id+"F13.opExtrude","SWEPT_BODY",BODY,{"disambiguationData":[OSD([sQuery(id+"F2.wireOp",EDGE,"E11"),sQuery(id+"F2.wireOp",EDGE,"E13"),sQuery(id+"F2.wireOp",EDGE,"E15"),sQuery(id+"F2.wireOp",EDGE,"E17"),sQuery(id+"F2.wireOp",EDGE,"E19"),sQuery(id+"F2.wireOp",EDGE,"E21"),sQuery(id+"F2.wireOp",EDGE,"E22"),sQuery(id+"F2.wireOp",EDGE,"E23"),sQuery(id+"F2.wireOp",EDGE,"E25"),sQuery(id+"F2.wireOp",EDGE,"E26"),sQuery(id+"F2.wireOp",EDGE,"E27"),sQuery(id+"F2.wireOp",EDGE,"E39.0"),sQuery(id+"F2.wireOp",EDGE,"E39.1"),sQuery(id+"F2.wireOp",EDGE,"E39.2"),sQuery(id+"F2.wireOp",EDGE,"E39.3"),sQuery(id+"F2.wireOp",EDGE,"E39.4"),sQuery(id+"F2.wireOp",EDGE,"E39.5")])]});
            hole(context, id + "F17", {"style" : HoleStyle.SIMPLE, "endStyle" : HoleEndStyle.BLIND, "oppositeDirection" : true, "standardTappedOrClearance" : lookupTablePath({ "standard" : "ANSI", "engagement" : "75%", "pitch" : "40 tpi", "size" : "#4", "type" : "Tapped" }), "standardBlindInLast" : lookupTablePath({ "standard" : "ANSI", "fit" : "Normal", "engagement" : "75%", "pitch" : "40 tpi", "size" : "#4", "type" : "Clearance & tapped" }), "holeDiameter" : 2.26 * mm, "majorDiameter" : 2.84 * mm, "showTappedDepth" : true, "holeDepth" : 12.7 * mm, "isTappedThrough" : true, "tappedDepth" : 10.8 * mm, "tapClearance" : 3, "locations" : qUnion([Q0, Q1]), "scope" : qUnion([Q2])});
        }
        {
            var Q0;
            Q0=makeQuery(id+"F2.imprint","IMPRINT",FACE,{"disambiguationData":[TD([[makeQuery(id+"F2.imprint","IMPRINT",EDGE,{"derivedFrom":sQuery(id+"F2.wireOp",EDGE,"E11")}),-1.0]])]});
            var Q1;
            Q1=makeQuery(id+"F2.imprint","IMPRINT",FACE,{"disambiguationData":[TD([[makeQuery(id+"F2.imprint","IMPRINT",EDGE,{"derivedFrom":sQuery(id+"F2.wireOp",EDGE,"E20")}),1.0]])]});
            var Q2;
            Q2=makeQuery(id+"F2.imprint","IMPRINT",FACE,{"disambiguationData":[TD([[makeQuery(id+"F2.imprint","IMPRINT",EDGE,{"derivedFrom":sQuery(id+"F2.wireOp",EDGE,"E29")}),1.0]])]});
            var Q3;
            Q3=makeQuery(id+"F2.imprint","IMPRINT",FACE,{"disambiguationData":[TD([[makeQuery(id+"F2.imprint","IMPRINT",EDGE,{"derivedFrom":sQuery(id+"F2.wireOp",EDGE,"E30")}),1.0]])]});
            var Q4;
            Q4=makeQuery(id+"F2.imprint","IMPRINT",FACE,{"disambiguationData":[TD([[makeQuery(id+"F2.imprint","IMPRINT",EDGE,{"derivedFrom":sQuery(id+"F2.wireOp",EDGE,"E28")}),1.0]])]});
            var Q5;
            Q5=makeQuery(id+"F2.imprint","IMPRINT",FACE,{"disambiguationData":[TD([[makeQuery(id+"F2.imprint","IMPRINT",EDGE,{"derivedFrom":sQuery(id+"F2.wireOp",EDGE,"E32")}),1.0]])]});
            var Q6;
            Q6=makeQuery(id+"F2.imprint","IMPRINT",FACE,{"disambiguationData":[TD([[makeQuery(id+"F2.imprint","IMPRINT",EDGE,{"derivedFrom":sQuery(id+"F2.wireOp",EDGE,"E31")}),1.0]])]});
            var Q7;
            Q7=makeQuery(id+"F2.imprint","IMPRINT",FACE,{"disambiguationData":[TD([[makeQuery(id+"F2.imprint","IMPRINT",EDGE,{"derivedFrom":sQuery(id+"F2.wireOp",EDGE,"E6")}),1.0]])]});
            var Q8;
            Q8=makeQuery(id+"F2.imprint","IMPRINT",FACE,{"disambiguationData":[TD([[makeQuery(id+"F2.imprint","IMPRINT",EDGE,{"derivedFrom":sQuery(id+"F2.wireOp",EDGE,"E8")}),-1.0]])]});
            var Q9;
            Q9=makeQuery(id+"F2.imprint","IMPRINT",FACE,{"disambiguationData":[TD([[makeQuery(id+"F2.imprint","IMPRINT",EDGE,{"derivedFrom":sQuery(id+"F2.wireOp",EDGE,"E4")}),-1.0]])]});
            var Q10;
            Q10=makeQuery(id+"F2.imprint","IMPRINT",FACE,{"disambiguationData":[TD([[makeQuery(id+"F2.imprint","IMPRINT",EDGE,{"derivedFrom":sQuery(id+"F2.wireOp",EDGE,"E10")}),-1.0]])]});
            var Q11;
            Q11=makeQuery(id+"F2.imprint","IMPRINT",FACE,{"disambiguationData":[TD([[makeQuery(id+"F2.imprint","IMPRINT",EDGE,{"derivedFrom":sQuery(id+"F2.wireOp",EDGE,"E5")}),-1.0]])]});
            var Q12;
            Q12=makeQuery(id+"F2.imprint","IMPRINT",FACE,{"disambiguationData":[TD([[makeQuery(id+"F2.imprint","IMPRINT",EDGE,{"derivedFrom":sQuery(id+"F2.wireOp",EDGE,"E6")}),-1.0]])]});
            var Q13;
            Q13=makeQuery(id+"F2.imprint","IMPRINT",FACE,{"disambiguationData":[TD([[makeQuery(id+"F2.imprint","IMPRINT",EDGE,{"derivedFrom":sQuery(id+"F2.wireOp",EDGE,"E5")}),1.0]])]});
            var Q14;
            Q14=makeQuery(id+"F2.imprint","IMPRINT",FACE,{"disambiguationData":[TD([[makeQuery(id+"F2.imprint","IMPRINT",EDGE,{"derivedFrom":sQuery(id+"F2.wireOp",EDGE,"E7")}),1.0]])]});
            var Q15;
            Q15=makeQuery(id+"F2.imprint","IMPRINT",FACE,{"disambiguationData":[TD([[makeQuery(id+"F2.imprint","IMPRINT",EDGE,{"derivedFrom":sQuery(id+"F2.wireOp",EDGE,"E10")}),1.0]])]});
            var Q16;
            Q16=makeQuery(id+"F2.imprint","IMPRINT",FACE,{"disambiguationData":[TD([[makeQuery(id+"F2.imprint","IMPRINT",EDGE,{"derivedFrom":sQuery(id+"F2.wireOp",EDGE,"E4")}),1.0]])]});
            var Q17;
            Q17=makeQuery(id+"F2.imprint","IMPRINT",FACE,{"disambiguationData":[TD([[makeQuery(id+"F2.imprint","IMPRINT",EDGE,{"derivedFrom":sQuery(id+"F2.wireOp",EDGE,"E7")}),-1.0]])]});
            var Q18;
            Q18=makeQuery(id+"F2.imprint","IMPRINT",FACE,{"disambiguationData":[TD([[makeQuery(id+"F2.imprint","IMPRINT",EDGE,{"derivedFrom":sQuery(id+"F2.wireOp",EDGE,"E9")}),-1.0]])]});
            var Q19;
            Q19=makeQuery(id+"F2.imprint","IMPRINT",FACE,{"disambiguationData":[TD([[makeQuery(id+"F2.imprint","IMPRINT",EDGE,{"derivedFrom":sQuery(id+"F2.wireOp",EDGE,"E3")}),-1.0]])]});
            var Q20;
            Q20=makeQuery(id+"F2.imprint","IMPRINT",FACE,{"disambiguationData":[TD([[makeQuery(id+"F2.imprint","IMPRINT",EDGE,{"derivedFrom":sQuery(id+"F2.wireOp",EDGE,"E3")}),1.0]])]});
            var Q21;
            Q21=makeQuery(id+"F2.imprint","IMPRINT",FACE,{"disambiguationData":[TD([[makeQuery(id+"F2.imprint","IMPRINT",EDGE,{"derivedFrom":sQuery(id+"F2.wireOp",EDGE,"E9")}),1.0]])]});
            var Q22;
            Q22=makeQuery(id+"F2.imprint","IMPRINT",FACE,{"disambiguationData":[TD([[makeQuery(id+"F2.imprint","IMPRINT",EDGE,{"derivedFrom":sQuery(id+"F2.wireOp",EDGE,"E8")}),1.0]])]});
            var Q23;
            Q23=makeQuery(id+"F2.imprint","IMPRINT",FACE,{"disambiguationData":[TD([[makeQuery(id+"F2.imprint","IMPRINT",EDGE,{"derivedFrom":sQuery(id+"F2.wireOp",EDGE,"E4")}),1.0]])]});
            var Q24;
            Q24=makeQuery(id+"F2.imprint","IMPRINT",FACE,{"disambiguationData":[TD([[makeQuery(id+"F2.imprint","IMPRINT",EDGE,{"derivedFrom":sQuery(id+"F2.wireOp",EDGE,"E10")}),1.0]])]});
            var Q25;
            Q25=makeQuery(id+"F2.imprint","IMPRINT",FACE,{"disambiguationData":[TD([[makeQuery(id+"F2.imprint","IMPRINT",EDGE,{"derivedFrom":sQuery(id+"F2.wireOp",EDGE,"E8")}),1.0]])]});
            var Q26;
            Q26=makeQuery(id+"F2.imprint","IMPRINT",FACE,{"disambiguationData":[TD([[makeQuery(id+"F2.imprint","IMPRINT",EDGE,{"derivedFrom":sQuery(id+"F2.wireOp",EDGE,"E6")}),1.0]])]});
            var Q27;
            Q27=makeQuery(id+"F2.imprint","IMPRINT",FACE,{"disambiguationData":[TD([[makeQuery(id+"F2.imprint","IMPRINT",EDGE,{"derivedFrom":sQuery(id+"F2.wireOp",EDGE,"E39.0")}),-1.0]])]});
            extrude(context, id + "F18", {"entities" : qUnion([Q0, Q1, Q2, Q3, Q4, Q5, Q6, Q7, Q8, Q9, Q10, Q11, Q12, Q13, Q14, Q15, Q16, Q17, Q18, Q19, Q20, Q21, Q22, Q23, Q24, Q25, Q26, Q27]), "depth" : 6.35 * mm, "offsetDistance" : 25.4 * mm});
        }
        {
            var Q0;
            Q0=makeQuery(id+"F2.imprint","IMPRINT",FACE,{"disambiguationData":[TD([[makeQuery(id+"F2.imprint","IMPRINT",EDGE,{"derivedFrom":sQuery(id+"F2.wireOp",EDGE,"E4")}),1.0]])]});
            var Q1;
            Q1=makeQuery(id+"F2.imprint","IMPRINT",FACE,{"disambiguationData":[TD([[makeQuery(id+"F2.imprint","IMPRINT",EDGE,{"derivedFrom":sQuery(id+"F2.wireOp",EDGE,"E6")}),1.0]])]});
            var Q2;
            Q2=makeQuery(id+"F2.imprint","IMPRINT",FACE,{"disambiguationData":[TD([[makeQuery(id+"F2.imprint","IMPRINT",EDGE,{"derivedFrom":sQuery(id+"F2.wireOp",EDGE,"E8")}),1.0]])]});
            var Q3;
            Q3=makeQuery(id+"F2.imprint","IMPRINT",FACE,{"disambiguationData":[TD([[makeQuery(id+"F2.imprint","IMPRINT",EDGE,{"derivedFrom":sQuery(id+"F2.wireOp",EDGE,"E10")}),1.0]])]});
            extrude(context, id + "F19", {"entities" : qUnion([Q0, Q1, Q2, Q3]), "operationType" : NewBodyOperationType.REMOVE, "depth" : 3.17 * mm, "offsetDistance" : 25.4 * mm});
        }
        {
            var Q0;
            Q0=sQuery(id+"F2.wireOp",VERTEX,"E2.4.0");
            var Q1;
            Q1=sQuery(id+"F2.wireOp",VERTEX,"E2.6.0");
            var Q2;
            Q2=sQuery(id+"F2.wireOp",VERTEX,"E1");
            var Q3;
            Q3=sQuery(id+"F2.wireOp",VERTEX,"E2.2.0");
            var Q4;
            Q4=makeQuery(id+"F18.opExtrude","SWEPT_BODY",BODY,{"disambiguationData":[OSD([sQuery(id+"F2.wireOp",EDGE,"E19")])]});
            hole(context, id + "F20", {"style" : HoleStyle.SIMPLE, "endStyle" : HoleEndStyle.THROUGH, "oppositeDirection" : true, "standardTappedOrClearance" : lookupTablePath({ "fit" : "Close (ASME)", "standard" : "ANSI", "size" : "#4", "type" : "Clearance" }), "standardBlindInLast" : lookupTablePath({ "fit" : "Close", "standard" : "ANSI", "engagement" : "75%", "pitch" : "40 tpi", "size" : "#4", "type" : "Clearance & tapped" }), "holeDiameter" : 3.05 * mm, "majorDiameter" : 6.35 * mm, "isTappedThrough" : true, "tappedDepth" : 12.7 * mm, "tapClearance" : 3, "locations" : qUnion([Q0, Q1, Q2, Q3]), "scope" : qUnion([Q4])});
        }
    });
